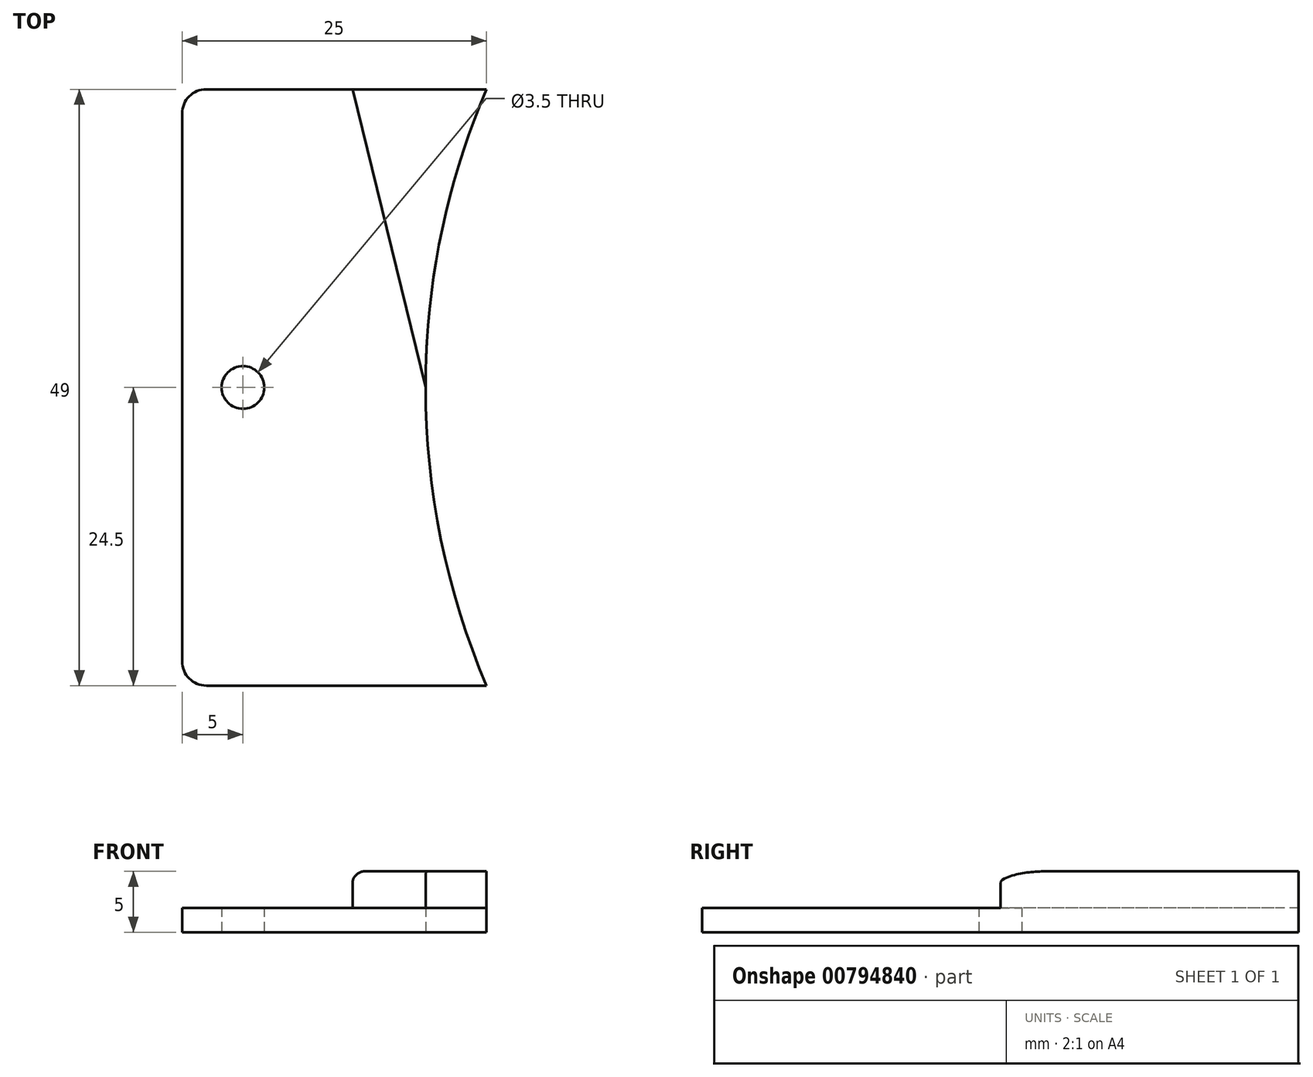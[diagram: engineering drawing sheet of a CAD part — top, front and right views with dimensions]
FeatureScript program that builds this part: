
annotation { "Feature Type Name" : "Feature", "Feature Type Description" : "" }
export const myFeature = defineFeature(function(context is Context, id is Id, definition is map)
    precondition{}
    {
        {
            var Q0;
            Q0=qCreatedBy(makeId("Top.planeOp"),FACE);
            var sketch = newSketch(context, id + "F0", { "sketchPlane" : qUnion([Q0])});
            skLineSegment(sketch, "E0", {"start": v(0, 0) * mm, "end": v(-100, 0) * mm, "construction": true});
            skLineSegment(sketch, "E1.bottom", {"start": v(-82.5, 24.5) * mm, "end": v(-32.5, 24.5) * mm});
            skLineSegment(sketch, "E1.top", {"start": v(-82.5, -24.5) * mm, "end": v(-32.5, -24.5) * mm});
            skLineSegment(sketch, "E1.left", {"start": v(-82.5, 24.5) * mm, "end": v(-82.5, -24.5) * mm});
            skLineSegment(sketch, "E1.right", {"start": v(-32.5, 24.5) * mm, "end": v(-32.5, -24.5) * mm});
            skPoint(sketch, "E1.middle", {"position": v(-57.5, 0) * mm});
            skCircle(sketch, "E2", {"center": v(0, 0) * mm, "radius": 62.5 * mm});
            skPoint(sketch, "E3", {"position": v(-68.5, 24.5) * mm});
            skPoint(sketch, "E4", {"position": v(-62.5, 0) * mm});
            skLineSegment(sketch, "E5", {"start": v(-68.5, 24.5) * mm, "end": v(-62.5, 0) * mm});
            skCircle(sketch, "E6", {"center": v(-77.5, 0) * mm, "radius": 1.75 * mm});
            skSolve(sketch);
        }
        {
            var Q0;
            {var subQ0=sQuery(id+"F0.wireOp",EDGE,"E5");Q0=makeQuery(id+"F0.imprint","IMPRINT",FACE,{"disambiguationData":[TD([[makeQuery(id+"F0.imprint","IMPRINT",EDGE,{"derivedFrom":subQ0}),1.0]])]});}
            extrude(context, id + "F1", {"entities" : qUnion([Q0]), "depth" : 5 * mm, "offsetDistance" : 25 * mm});
        }
        {
            var Q0;
            {var subQ4=sQuery(id+"F0.wireOp",EDGE,"E1.left");Q0=makeQuery(id+"F0.imprint","IMPRINT",FACE,{"disambiguationData":[TD([[makeQuery(id+"F0.imprint","IMPRINT",EDGE,{"derivedFrom":subQ4}),1.0]])]});}
            extrude(context, id + "F2", {"entities" : qUnion([Q0]), "operationType" : NewBodyOperationType.ADD, "depth" : 2 * mm, "offsetDistance" : 25 * mm});
        }
        {
            var Q0;
            Q0=makeQuery(id+"F2.opExtrude","SWEPT_EDGE",EDGE,{"disambiguationData":[OSD([sQuery(id+"F0.wireOp",EDGE,"E1.top"),sQuery(id+"F0.wireOp",EDGE,"E1.left")])]});
            var Q1;
            Q1=makeQuery(id+"F2.opExtrude","SWEPT_EDGE",EDGE,{"disambiguationData":[OSD([sQuery(id+"F0.wireOp",EDGE,"E1.bottom"),sQuery(id+"F0.wireOp",EDGE,"E1.left")])]});
            fillet(context, id + "F3", {"entities" : qUnion([Q0, Q1]), "radius" : 2 * mm, "tangentPropagation" : true, "allowEdgeOverflow" : false});
        }
        {
            var Q0;
            Q0=makeQuery(id+"F1.opExtrude","CAP_EDGE",EDGE,{"disambiguationData":[OSD([sQuery(id+"F0.wireOp",EDGE,"E5")])],"isStart":false});
            fillet(context, id + "F4", {"entities" : qUnion([Q0]), "radius" : 1 * mm, "tangentPropagation" : true, "allowEdgeOverflow" : false});
        }
    });
